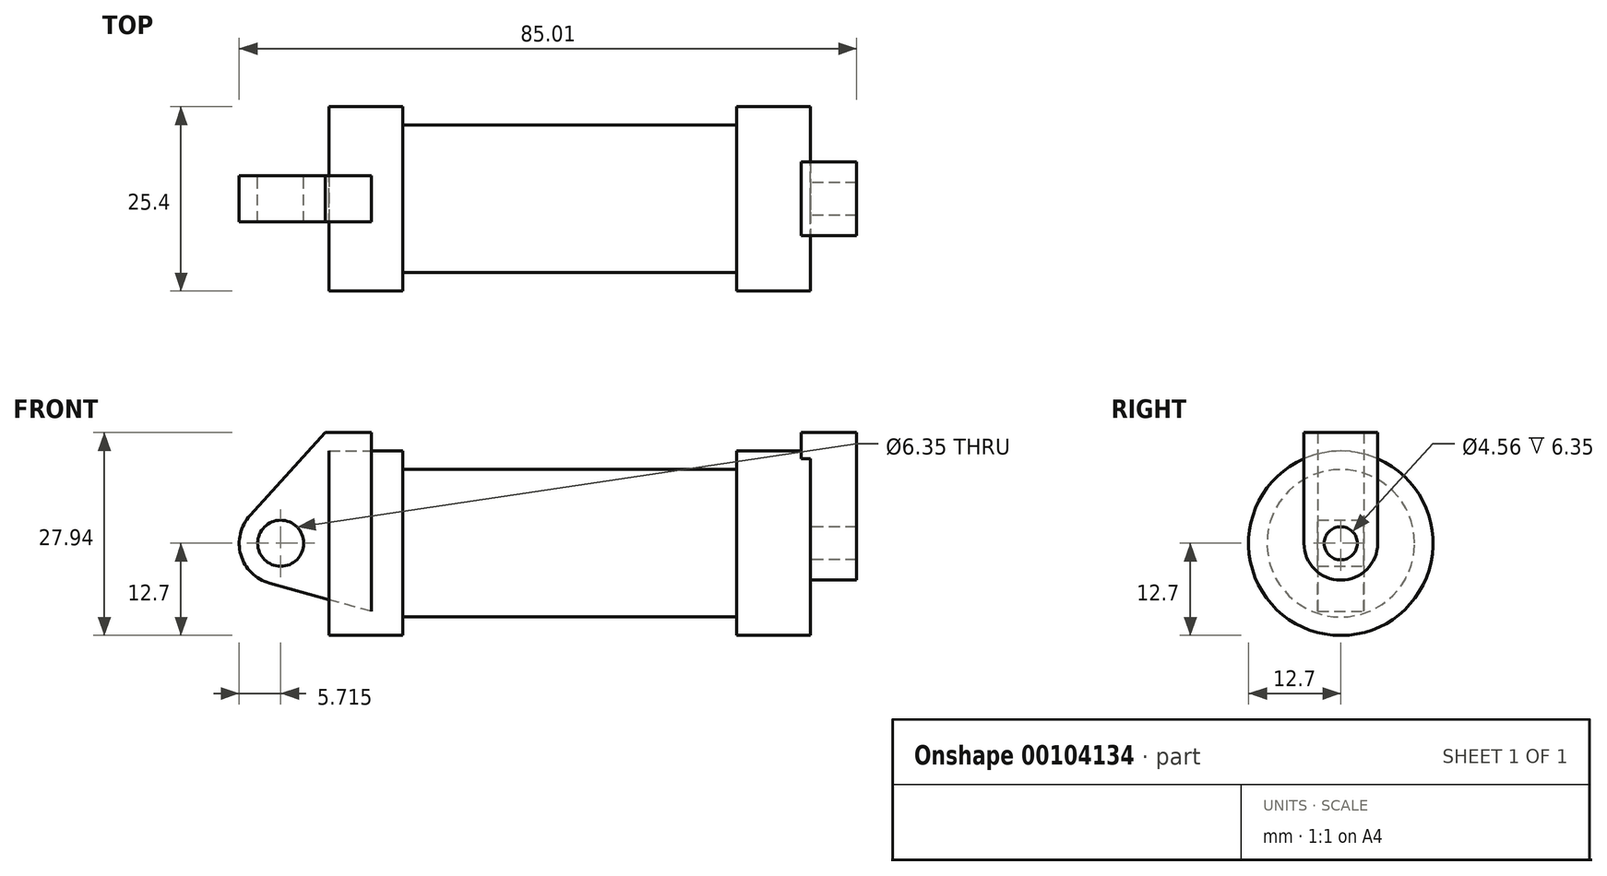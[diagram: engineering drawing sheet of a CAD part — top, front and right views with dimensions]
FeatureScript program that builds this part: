
annotation { "Feature Type Name" : "Feature", "Feature Type Description" : "" }
export const myFeature = defineFeature(function(context is Context, id is Id, definition is map)
    precondition{}
    {
        {
            var Q0;
            Q0=qCreatedBy(makeId("Front.planeOp"),FACE);
            var sketch = newSketch(context, id + "F0", { "sketchPlane" : qUnion([Q0])});
            skLineSegment(sketch, "E0", {"start": v(0, 0) * mm, "end": v(0, 12.7) * mm});
            skLineSegment(sketch, "E1", {"start": v(0, 12.7) * mm, "end": v(10.16, 12.7) * mm});
            skLineSegment(sketch, "E2", {"start": v(10.16, 12.7) * mm, "end": v(10.16, 10.16) * mm});
            skLineSegment(sketch, "E3", {"start": v(10.16, 10.16) * mm, "end": v(56.13, 10.16) * mm});
            skLineSegment(sketch, "E4", {"start": v(56.13, 10.16) * mm, "end": v(56.13, 12.7) * mm});
            skLineSegment(sketch, "E5", {"start": v(56.13, 12.7) * mm, "end": v(66.3, 12.7) * mm});
            skLineSegment(sketch, "E6", {"start": v(66.3, 12.7) * mm, "end": v(66.3, 0) * mm});
            skLineSegment(sketch, "E7", {"start": v(66.3, 0) * mm, "end": v(0, 0) * mm});
            skLineSegment(sketch, "E8", {"start": v(5.84, 15.24) * mm, "end": v(-0.5, 15.24) * mm});
            skLineSegment(sketch, "E9", {"start": v(-0.5, 15.24) * mm, "end": v(-10.88, 3.85) * mm});
            skLineSegment(sketch, "E10", {"start": v(0, 0) * mm, "end": v(-6.65, 0) * mm});
            skCircle(sketch, "E11", {"center": v(-6.65, 0) * mm, "radius": 5.72 * mm});
            skCircle(sketch, "E12", {"center": v(-6.65, 0) * mm, "radius": 3.18 * mm});
            skLineSegment(sketch, "E13", {"start": v(5.84, 15.24) * mm, "end": v(5.84, -9.4) * mm});
            skLineSegment(sketch, "E14", {"start": v(5.84, -9.4) * mm, "end": v(-8.18, -5.5) * mm});
            skSolve(sketch);
        }
        {
            var Q0;
            {var subQ0=sQuery(id+"F0.wireOp",EDGE,"E2");Q0=makeQuery(id+"F0.imprint","IMPRINT",FACE,{"disambiguationData":[TD([[makeQuery(id+"F0.imprint","IMPRINT",EDGE,{"derivedFrom":subQ0}),-1.0]])]});}
            var Q1;
            {var subQ0=sQuery(id+"F0.wireOp",EDGE,"E0");Q1=makeQuery(id+"F0.imprint","IMPRINT",FACE,{"disambiguationData":[TD([[makeQuery(id+"F0.imprint","IMPRINT",EDGE,{"derivedFrom":subQ0}),-1.0]])]});}
            var Q2;
            Q2=sQuery(id+"F0.wireOp",EDGE,"E0");
            var Q3;
            Q3=sQuery(id+"F0.wireOp",EDGE,"E1");
            var Q4;
            Q4=sQuery(id+"F0.wireOp",EDGE,"E2");
            var Q5;
            Q5=sQuery(id+"F0.wireOp",EDGE,"E3");
            var Q6;
            Q6=sQuery(id+"F0.wireOp",EDGE,"E5");
            var Q7;
            Q7=sQuery(id+"F0.wireOp",EDGE,"E6");
            var Q8;
            Q8=sQuery(id+"F0.wireOp",EDGE,"E7");
            revolve(context, id + "F1", {"entities" : qUnion([Q0, Q1]), "surfaceEntities" : qUnion([Q2, Q3, Q4, Q5, Q6, Q7]), "axis" : qUnion([Q8]), "revolveType" : RevolveType.FULL});
        }
        {
            var Q0;
            {var subQ3=sQuery(id+"F0.wireOp",EDGE,"E0");Q0=makeQuery(id+"F0.imprint","IMPRINT",FACE,{"disambiguationData":[TD([[makeQuery(id+"F0.imprint","IMPRINT",EDGE,{"derivedFrom":subQ3}),1.0]])]});}
            var Q1;
            {var subQ0=sQuery(id+"F0.wireOp",EDGE,"E0");Q1=makeQuery(id+"F0.imprint","IMPRINT",FACE,{"disambiguationData":[TD([[makeQuery(id+"F0.imprint","IMPRINT",EDGE,{"derivedFrom":subQ0}),-1.0]])]});}
            var Q2;
            {var subQ0=sQuery(id+"F0.wireOp",EDGE,"E14");Q2=makeQuery(id+"F0.imprint","IMPRINT",FACE,{"disambiguationData":[TD([[makeQuery(id+"F0.imprint","IMPRINT",EDGE,{"derivedFrom":subQ0}),-1.0]])]});}
            var Q3;
            {var subQ4=sQuery(id+"F0.wireOp",EDGE,"E12");Q3=makeQuery(id+"F0.imprint","IMPRINT",FACE,{"disambiguationData":[TD([[makeQuery(id+"F0.imprint","IMPRINT",EDGE,{"derivedFrom":subQ4}),-1.0]])]});}
            extrude(context, id + "F2", {"entities" : qUnion([Q0, Q1, Q2, Q3]), "endBound" : BoundingType.SYMMETRIC, "depth" : 6.35 * mm});
        }
        {
            var Q0;
            Q0=makeQuery(id+"F1.opRevolve","SWEPT_FACE",FACE,{"disambiguationData":[OSD([sQuery(id+"F0.wireOp",EDGE,"E6")])]});
            var sketch = newSketch(context, id + "F3", { "sketchPlane" : qUnion([Q0])});
            skCircle(sketch, "E15", {"center": v(0, 0) * mm, "radius": 5.08 * mm});
            skCircle(sketch, "E16", {"center": v(0, 0) * mm, "radius": 2.28 * mm});
            skLineSegment(sketch, "E17", {"start": v(-5.08, 0) * mm, "end": v(-5.08, 15.24) * mm});
            skLineSegment(sketch, "E18", {"start": v(-5.08, 15.24) * mm, "end": v(5.08, 15.24) * mm});
            skLineSegment(sketch, "E19", {"start": v(5.08, 0) * mm, "end": v(5.08, 15.24) * mm});
            skSolve(sketch);
        }
        {
            var Q0;
            Q0 = qSketchRegion(id + "F3", true);
            extrude(context, id + "F4", {"entities" : qUnion([Q0]), "operationType" : NewBodyOperationType.ADD, "depth" : 6.35 * mm, "hasSecondDirection" : true, "secondDirectionOppositeDirection" : true, "secondDirectionDepth" : 1.27 * mm});
        }
    });
